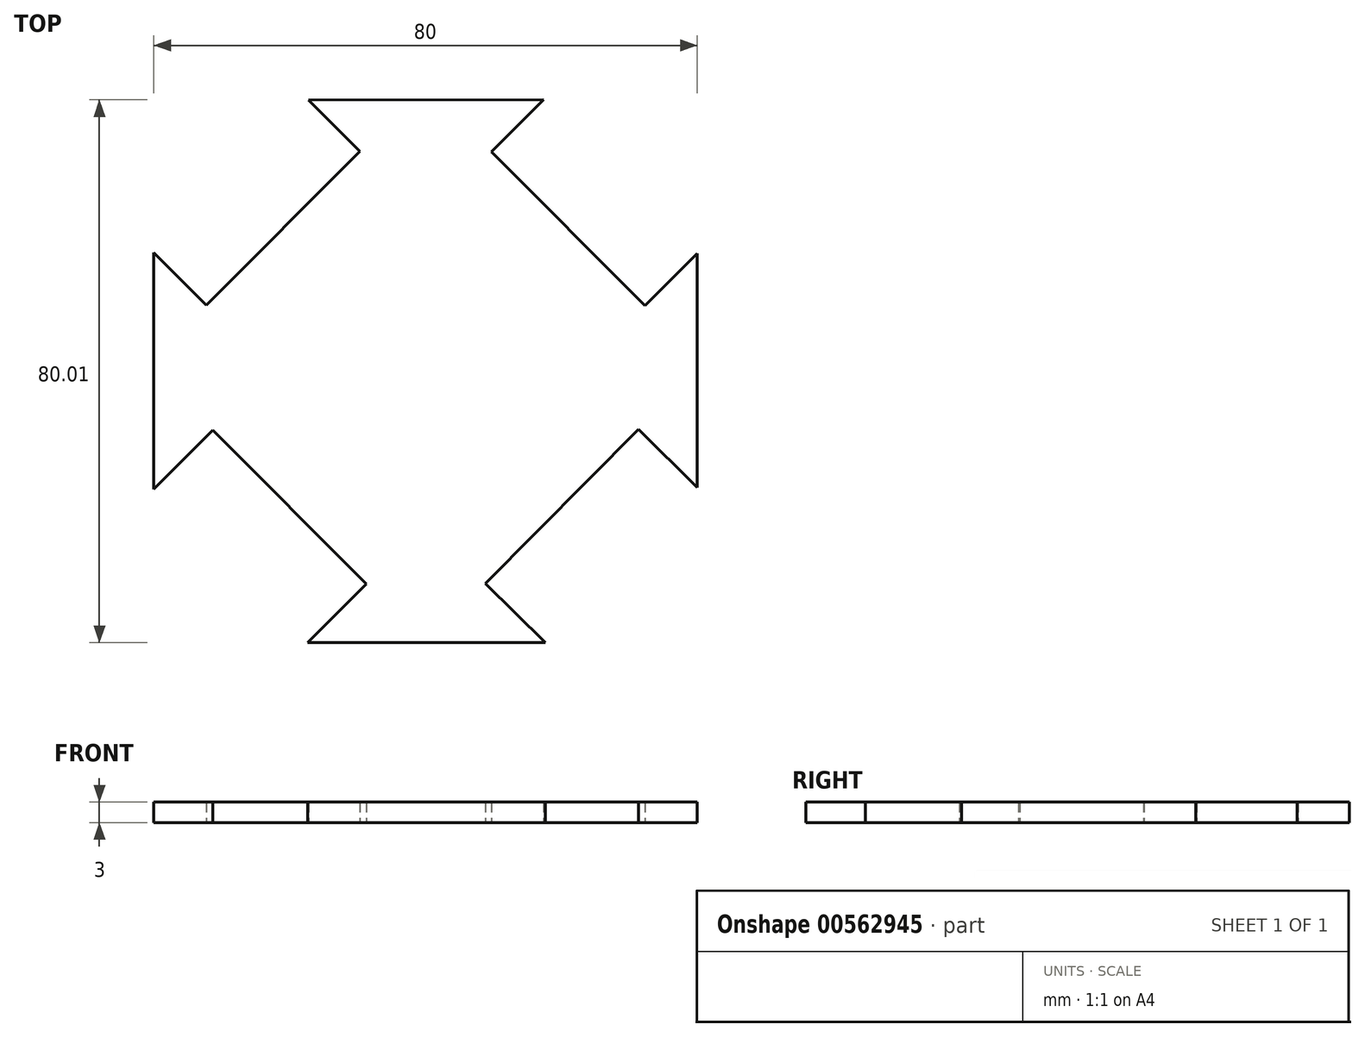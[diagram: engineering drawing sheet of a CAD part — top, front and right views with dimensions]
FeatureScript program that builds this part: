
annotation { "Feature Type Name" : "Feature", "Feature Type Description" : "" }
export const myFeature = defineFeature(function(context is Context, id is Id, definition is map)
    precondition{}
    {
        {
            var Q0;
            Q0=qCreatedBy(makeId("Top.planeOp"),FACE);
            var sketch = newSketch(context, id + "F0", { "sketchPlane" : qUnion([Q0])});
            skCircle(sketch, "E0", {"center": v(-0.03, 1.02) * mm, "radius": 105 * mm});
            skCircle(sketch, "E1", {"center": v(-29.75, 90.8) * mm, "radius": 6.5 * mm});
            skCircle(sketch, "E2", {"center": v(29.27, 90.8) * mm, "radius": 6.5 * mm});
            skCircle(sketch, "E3", {"center": v(-91.34, -22.45) * mm, "radius": 6.5 * mm});
            skCircle(sketch, "E4", {"center": v(91.29, -22.45) * mm, "radius": 6.5 * mm});
            skLineSegment(sketch, "E5", {"start": v(-26.15, -74.78) * mm, "end": v(26.1, -74.78) * mm});
            skLineSegment(sketch, "E6", {"start": v(-26.15, -74.78) * mm, "end": v(-45.16, -93.79) * mm});
            skLineSegment(sketch, "E7", {"start": v(26.1, -74.78) * mm, "end": v(45.1, -93.79) * mm});
            skLineSegment(sketch, "E8", {"start": v(-20.96, 21.1) * mm, "end": v(-32.26, 9.77) * mm});
            skLineSegment(sketch, "E9", {"start": v(-20.96, 21.1) * mm, "end": v(-9.66, 32.42) * mm});
            skLineSegment(sketch, "E10", {"start": v(21, 21) * mm, "end": v(9.68, 32.31) * mm});
            skLineSegment(sketch, "E11", {"start": v(9.68, 32.31) * mm, "end": v(32.31, 9.68) * mm});
            skLineSegment(sketch, "E12", {"start": v(-20, -20) * mm, "end": v(-31.32, -8.7) * mm});
            skLineSegment(sketch, "E13", {"start": v(-20, -20) * mm, "end": v(-8.7, -31.32) * mm});
            skLineSegment(sketch, "E14", {"start": v(20.08, -19.9) * mm, "end": v(31.34, -8.52) * mm});
            skLineSegment(sketch, "E15", {"start": v(31.34, -8.52) * mm, "end": v(20.08, -19.9) * mm});
            skLineSegment(sketch, "E16", {"start": v(20.08, -19.9) * mm, "end": v(8.82, -31.26) * mm});
            skLineSegment(sketch, "E17.bottom", {"start": v(-82.14, 0) * mm, "end": v(-68.14, 0) * mm});
            skLineSegment(sketch, "E17.top", {"start": v(-82.14, 20) * mm, "end": v(-68.14, 20) * mm});
            skLineSegment(sketch, "E17.left", {"start": v(-85.14, 3) * mm, "end": v(-85.14, 17) * mm});
            skLineSegment(sketch, "E17.right", {"start": v(-65.14, 3) * mm, "end": v(-65.14, 17) * mm});
            skLineSegment(sketch, "E18.bottom", {"start": v(82.1, 0) * mm, "end": v(68.1, 0) * mm});
            skLineSegment(sketch, "E18.top", {"start": v(82.1, 20) * mm, "end": v(68.1, 20) * mm});
            skLineSegment(sketch, "E18.left", {"start": v(85.1, 3) * mm, "end": v(85.1, 17) * mm});
            skLineSegment(sketch, "E18.right", {"start": v(65.1, 3) * mm, "end": v(65.1, 17) * mm});
            skPoint(sketch, "E19.visualSharp", {"position": v(-85.14, 20) * mm});
            skArc(sketch, "E19.filletArc", {"start": v(-82.14, 20) * mm, "mid": v(-84.26, 19.12) * mm, "end": v(-85.14, 17) * mm});
            skPoint(sketch, "E20.visualSharp", {"position": v(-65.14, 20) * mm});
            skArc(sketch, "E20.filletArc", {"start": v(-65.14, 17) * mm, "mid": v(-66.01, 19.12) * mm, "end": v(-68.14, 20) * mm});
            skPoint(sketch, "E21.visualSharp", {"position": v(-65.14, 0) * mm});
            skArc(sketch, "E21.filletArc", {"start": v(-68.14, 0) * mm, "mid": v(-66.01, 0.88) * mm, "end": v(-65.14, 3) * mm});
            skPoint(sketch, "E22.visualSharp", {"position": v(-85.14, 0) * mm});
            skArc(sketch, "E22.filletArc", {"start": v(-85.14, 3) * mm, "mid": v(-84.26, 0.88) * mm, "end": v(-82.14, 0) * mm});
            skPoint(sketch, "E23.visualSharp", {"position": v(65.1, 0) * mm});
            skArc(sketch, "E23.filletArc", {"start": v(65.1, 3) * mm, "mid": v(65.98, 0.88) * mm, "end": v(68.1, 0) * mm});
            skPoint(sketch, "E24.visualSharp", {"position": v(65.1, 20) * mm});
            skArc(sketch, "E24.filletArc", {"start": v(68.1, 20) * mm, "mid": v(65.98, 19.12) * mm, "end": v(65.1, 17) * mm});
            skPoint(sketch, "E25.visualSharp", {"position": v(85.1, 20) * mm});
            skArc(sketch, "E25.filletArc", {"start": v(85.1, 17) * mm, "mid": v(84.23, 19.12) * mm, "end": v(82.1, 20) * mm});
            skPoint(sketch, "E26.visualSharp", {"position": v(85.1, 0) * mm});
            skArc(sketch, "E26.filletArc", {"start": v(82.1, 0) * mm, "mid": v(84.23, 0.88) * mm, "end": v(85.1, 3) * mm});
            skLineSegment(sketch, "E27", {"start": v(50.85, -72.9) * mm, "end": v(37.6, -86.28) * mm});
            skLineSegment(sketch, "E28", {"start": v(73.53, -50.31) * mm, "end": v(87.6, -36.1) * mm});
            skLineSegment(sketch, "E29", {"start": v(87.6, -36.1) * mm, "end": v(95.07, -43.5) * mm});
            skLineSegment(sketch, "E30", {"start": v(50.85, -72.9) * mm, "end": v(8.82, -31.26) * mm});
            skLineSegment(sketch, "E31", {"start": v(31.34, -8.52) * mm, "end": v(73.53, -50.31) * mm});
            skLineSegment(sketch, "E32", {"start": v(-50.53, -73.16) * mm, "end": v(-37.53, -86.16) * mm});
            skLineSegment(sketch, "E33", {"start": v(-73.32, -50.69) * mm, "end": v(-87.46, -36.55) * mm});
            skLineSegment(sketch, "E34", {"start": v(-87.46, -36.55) * mm, "end": v(-94.9, -43.98) * mm});
            skLineSegment(sketch, "E35", {"start": v(-73.32, -50.69) * mm, "end": v(-31.32, -8.7) * mm});
            skLineSegment(sketch, "E36", {"start": v(-8.7, -31.32) * mm, "end": v(-50.53, -73.16) * mm});
            skLineSegment(sketch, "E37", {"start": v(-74.16, 51.56) * mm, "end": v(-88.28, 37.4) * mm});
            skLineSegment(sketch, "E38", {"start": v(-88.28, 37.4) * mm, "end": v(-95.54, 44.64) * mm});
            skLineSegment(sketch, "E39", {"start": v(-51.69, 74.34) * mm, "end": v(-37.56, 88.5) * mm});
            skLineSegment(sketch, "E40", {"start": v(-37.56, 88.5) * mm, "end": v(-44.98, 95.9) * mm});
            skLineSegment(sketch, "E41", {"start": v(-51.69, 74.34) * mm, "end": v(-9.66, 32.42) * mm});
            skLineSegment(sketch, "E42", {"start": v(-74.16, 51.56) * mm, "end": v(-32.26, 9.77) * mm});
            skLineSegment(sketch, "E43", {"start": v(51.68, 74.3) * mm, "end": v(37.54, 88.45) * mm});
            skPoint(sketch, "E44.endSnap0", {"position": v(44.6, 81.38) * mm});
            skPoint(sketch, "E45.endSnap0", {"position": v(0, 51.52) * mm});
            skLineSegment(sketch, "E46", {"start": v(74.14, 51.52) * mm, "end": v(88.29, 37.38) * mm});
            skLineSegment(sketch, "E47", {"start": v(51.68, 74.3) * mm, "end": v(9.68, 32.31) * mm});
            skLineSegment(sketch, "E48", {"start": v(74.14, 51.52) * mm, "end": v(32.31, 9.68) * mm});
            skLineSegment(sketch, "E49", {"start": v(0, 74.3) * mm, "end": v(7, 74.3) * mm});
            skLineSegment(sketch, "E50", {"start": v(10, 71.3) * mm, "end": v(10, 57.3) * mm});
            skLineSegment(sketch, "E51", {"start": v(7, 54.3) * mm, "end": v(-7, 54.3) * mm});
            skLineSegment(sketch, "E52", {"start": v(-10, 57.3) * mm, "end": v(-10, 71.3) * mm});
            skLineSegment(sketch, "E53", {"start": v(-7, 74.3) * mm, "end": v(0, 74.3) * mm});
            skPoint(sketch, "E54.visualSharp", {"position": v(-10, 74.3) * mm});
            skArc(sketch, "E54.filletArc", {"start": v(-7, 74.3) * mm, "mid": v(-9.12, 73.43) * mm, "end": v(-10, 71.3) * mm});
            skPoint(sketch, "E55.visualSharp", {"position": v(10, 74.3) * mm});
            skArc(sketch, "E55.filletArc", {"start": v(10, 71.3) * mm, "mid": v(9.12, 73.43) * mm, "end": v(7, 74.3) * mm});
            skPoint(sketch, "E56.visualSharp", {"position": v(10, 54.3) * mm});
            skArc(sketch, "E56.filletArc", {"start": v(7, 54.3) * mm, "mid": v(9.12, 55.18) * mm, "end": v(10, 57.3) * mm});
            skPoint(sketch, "E57.visualSharp", {"position": v(-10, 54.3) * mm});
            skArc(sketch, "E57.filletArc", {"start": v(-10, 57.3) * mm, "mid": v(-9.12, 55.18) * mm, "end": v(-7, 54.3) * mm});
            skLineSegment(sketch, "E58", {"start": v(32.31, 9.68) * mm, "end": v(74.14, 51.52) * mm});
            skLineSegment(sketch, "E59", {"start": v(88.29, 37.38) * mm, "end": v(95.5, 44.6) * mm});
            skLineSegment(sketch, "E60", {"start": v(37.54, 88.45) * mm, "end": v(44.97, 95.88) * mm});
            skLineSegment(sketch, "E61", {"start": v(0, 40) * mm, "end": v(17.38, 40) * mm});
            skLineSegment(sketch, "E62", {"start": v(17.38, 40) * mm, "end": v(-17.25, 40) * mm});
            skLineSegment(sketch, "E63", {"start": v(0, -40) * mm, "end": v(17.65, -40) * mm});
            skLineSegment(sketch, "E64", {"start": v(17.65, -40) * mm, "end": v(-17.37, -40) * mm});
            skLineSegment(sketch, "E65", {"start": v(-40, 0) * mm, "end": v(-40, 17.5) * mm});
            skLineSegment(sketch, "E66", {"start": v(-40, 17.5) * mm, "end": v(-40, -17.37) * mm});
            skLineSegment(sketch, "E67", {"start": v(40, 0) * mm, "end": v(40, 17.37) * mm});
            skLineSegment(sketch, "E68", {"start": v(40, 17.37) * mm, "end": v(40, -17.1) * mm});
            skSolve(sketch);
        }
        {
            var Q0;
            {var subQ6=sQuery(id+"F0.wireOp",EDGE,"E8");Q0=makeQuery(id+"F0.imprint","IMPRINT",FACE,{"disambiguationData":[TD([[makeQuery(id+"F0.imprint","IMPRINT",EDGE,{"derivedFrom":subQ6}),1.0]])]});}
            extrude(context, id + "F1", {"entities" : qUnion([Q0]), "depth" : 3 * mm, "offsetDistance" : 25.4 * mm});
        }
    });
